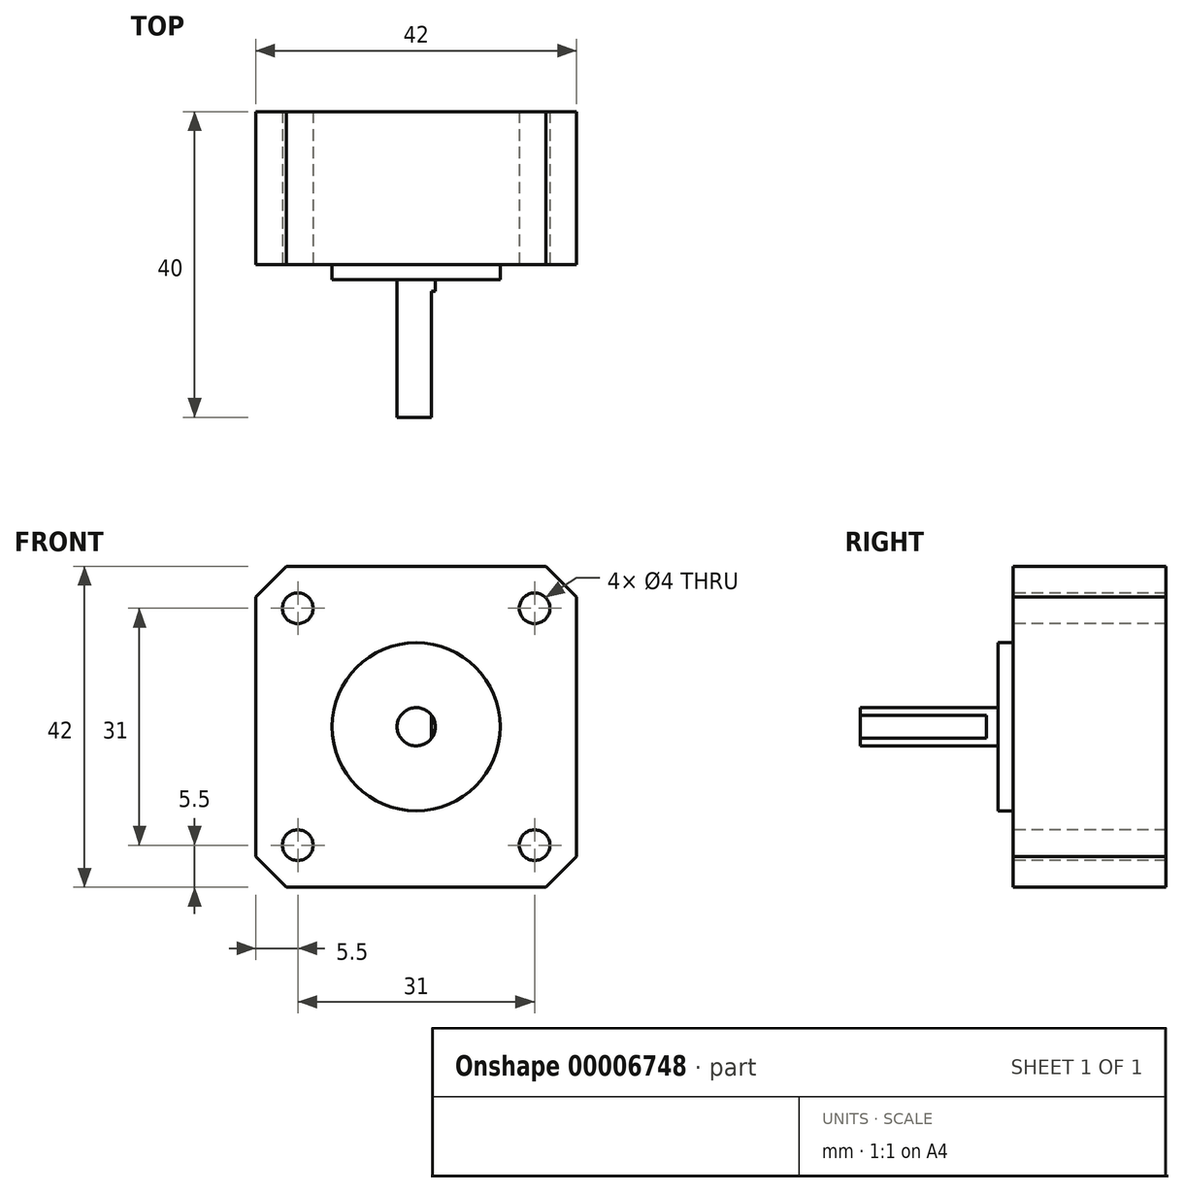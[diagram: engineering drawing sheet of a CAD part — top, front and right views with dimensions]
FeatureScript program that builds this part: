
annotation { "Feature Type Name" : "Feature", "Feature Type Description" : "" }
export const myFeature = defineFeature(function(context is Context, id is Id, definition is map)
    precondition{}
    {
        {
            var Q0;
            Q0=qCreatedBy(makeId("Front.planeOp"),FACE);
            var sketch = newSketch(context, id + "F0", { "sketchPlane" : qUnion([Q0])});
            skLineSegment(sketch, "E0.bottom", {"start": v(-21, -21) * mm, "end": v(21, -21) * mm});
            skLineSegment(sketch, "E0.top", {"start": v(-21, 21) * mm, "end": v(21, 21) * mm});
            skLineSegment(sketch, "E0.left", {"start": v(-21, -21) * mm, "end": v(-21, 21) * mm});
            skLineSegment(sketch, "E0.right", {"start": v(21, -21) * mm, "end": v(21, 21) * mm});
            skPoint(sketch, "E0.middle", {"position": v(0, 0) * mm});
            skCircle(sketch, "E1", {"center": v(-15.5, 15.5) * mm, "radius": 2 * mm});
            skCircle(sketch, "E2", {"center": v(15.5, 15.5) * mm, "radius": 2 * mm});
            skCircle(sketch, "E3", {"center": v(15.5, -15.5) * mm, "radius": 2 * mm});
            skCircle(sketch, "E4", {"center": v(-15.5, -15.5) * mm, "radius": 2 * mm});
            skLineSegment(sketch, "E5", {"start": v(-15.5, 15.5) * mm, "end": v(15.5, -15.5) * mm, "construction": true});
            skLineSegment(sketch, "E6", {"start": v(-15.5, 15.5) * mm, "end": v(15.5, 15.5) * mm, "construction": true});
            skLineSegment(sketch, "E7", {"start": v(15.5, 15.5) * mm, "end": v(15.5, -15.5) * mm, "construction": true});
            skCircle(sketch, "E8", {"center": v(0, 0) * mm, "radius": 11 * mm});
            skCircle(sketch, "E9", {"center": v(0, 0) * mm, "radius": 2.5 * mm});
            skCircle(sketch, "E10", {"center": v(0, 0) * mm, "radius": 4.1 * mm});
            skLineSegment(sketch, "E11", {"start": v(2, 1.5) * mm, "end": v(2, -1.5) * mm});
            skSolve(sketch);
        }
        {
            var Q0;
            Q0=makeQuery(id+"F0.imprint","IMPRINT",FACE,{"disambiguationData":[TD([[makeQuery(id+"F0.imprint","IMPRINT",EDGE,{"derivedFrom":sQuery(id+"F0.wireOp",EDGE,"E0.bottom")}),1.0]])]});
            var Q1;
            Q1=makeQuery(id+"F0.imprint","IMPRINT",FACE,{"disambiguationData":[TD([[makeQuery(id+"F0.imprint","IMPRINT",EDGE,{"derivedFrom":sQuery(id+"F0.wireOp",EDGE,"E8")}),1.0]])]});
            var Q2;
            {var subQ0=sQuery(id+"F0.wireOp",EDGE,"E11");Q2=makeQuery(id+"F0.imprint","IMPRINT",FACE,{"disambiguationData":[TD([[makeQuery(id+"F0.imprint","IMPRINT",EDGE,{"derivedFrom":subQ0}),-1.0]])]});}
            var Q3;
            {var subQ0=sQuery(id+"F0.wireOp",EDGE,"E11");Q3=makeQuery(id+"F0.imprint","IMPRINT",FACE,{"disambiguationData":[TD([[makeQuery(id+"F0.imprint","IMPRINT",EDGE,{"derivedFrom":subQ0}),1.0]])]});}
            var Q4;
            Q4=makeQuery(id+"F0.imprint","IMPRINT",FACE,{"disambiguationData":[TD([[makeQuery(id+"F0.imprint","IMPRINT",EDGE,{"derivedFrom":sQuery(id+"F0.wireOp",EDGE,"E10")}),1.0]])]});
            extrude(context, id + "F1", {"entities" : qUnion([Q0, Q1, Q2, Q3, Q4]), "oppositeDirection" : true, "depth" : 20 * mm, "offsetDistance" : 25 * mm});
        }
        {
            var Q0;
            Q0=makeQuery(id+"F0.imprint","IMPRINT",FACE,{"disambiguationData":[TD([[makeQuery(id+"F0.imprint","IMPRINT",EDGE,{"derivedFrom":sQuery(id+"F0.wireOp",EDGE,"E8")}),1.0]])]});
            var Q1;
            Q1=makeQuery(id+"F0.imprint","IMPRINT",FACE,{"disambiguationData":[TD([[makeQuery(id+"F0.imprint","IMPRINT",EDGE,{"derivedFrom":sQuery(id+"F0.wireOp",EDGE,"E10")}),1.0]])]});
            var Q2;
            {var subQ0=sQuery(id+"F0.wireOp",EDGE,"E11");Q2=makeQuery(id+"F0.imprint","IMPRINT",FACE,{"disambiguationData":[TD([[makeQuery(id+"F0.imprint","IMPRINT",EDGE,{"derivedFrom":subQ0}),-1.0]])]});}
            var Q3;
            {var subQ0=sQuery(id+"F0.wireOp",EDGE,"E11");Q3=makeQuery(id+"F0.imprint","IMPRINT",FACE,{"disambiguationData":[TD([[makeQuery(id+"F0.imprint","IMPRINT",EDGE,{"derivedFrom":subQ0}),1.0]])]});}
            extrude(context, id + "F2", {"entities" : qUnion([Q0, Q1, Q2, Q3]), "operationType" : NewBodyOperationType.ADD, "depth" : 2 * mm, "offsetDistance" : 25 * mm});
        }
        {
            var Q0;
            {var subQ0=sQuery(id+"F0.wireOp",EDGE,"E11");Q0=makeQuery(id+"F0.imprint","IMPRINT",FACE,{"disambiguationData":[TD([[makeQuery(id+"F0.imprint","IMPRINT",EDGE,{"derivedFrom":subQ0}),-1.0]])]});}
            var Q1;
            {var subQ0=sQuery(id+"F0.wireOp",EDGE,"E11");Q1=makeQuery(id+"F0.imprint","IMPRINT",FACE,{"disambiguationData":[TD([[makeQuery(id+"F0.imprint","IMPRINT",EDGE,{"derivedFrom":subQ0}),1.0]])]});}
            extrude(context, id + "F3", {"entities" : qUnion([Q0, Q1]), "operationType" : NewBodyOperationType.ADD, "depth" : 3.5 * mm, "offsetDistance" : 25 * mm});
        }
        {
            var Q0;
            {var subQ0=sQuery(id+"F0.wireOp",EDGE,"E11");Q0=makeQuery(id+"F0.imprint","IMPRINT",FACE,{"disambiguationData":[TD([[makeQuery(id+"F0.imprint","IMPRINT",EDGE,{"derivedFrom":subQ0}),-1.0]])]});}
            extrude(context, id + "F4", {"entities" : qUnion([Q0]), "operationType" : NewBodyOperationType.ADD, "depth" : 20 * mm, "offsetDistance" : 25 * mm});
        }
        {
            var Q0;
            Q0=makeQuery(id+"F1.opExtrude","SWEPT_EDGE",EDGE,{"disambiguationData":[OSD([sQuery(id+"F0.wireOp",EDGE,"E0.top"),sQuery(id+"F0.wireOp",EDGE,"E0.left")])]});
            var Q1;
            Q1=makeQuery(id+"F1.opExtrude","SWEPT_EDGE",EDGE,{"disambiguationData":[OSD([sQuery(id+"F0.wireOp",EDGE,"E0.top"),sQuery(id+"F0.wireOp",EDGE,"E0.right")])]});
            var Q2;
            Q2=makeQuery(id+"F1.opExtrude","SWEPT_EDGE",EDGE,{"disambiguationData":[OSD([sQuery(id+"F0.wireOp",EDGE,"E0.bottom"),sQuery(id+"F0.wireOp",EDGE,"E0.right")])]});
            var Q3;
            Q3=makeQuery(id+"F1.opExtrude","SWEPT_EDGE",EDGE,{"disambiguationData":[OSD([sQuery(id+"F0.wireOp",EDGE,"E0.bottom"),sQuery(id+"F0.wireOp",EDGE,"E0.left")])]});
            chamfer(context, id + "F5", {"entities" : qUnion([Q0, Q1, Q2, Q3]), "width" : 4 * mm, "tangentPropagation" : true});
        }
    });
